# Revit family: Shower-Rainhead-KOHLER-WaterTile-K-98740_1
name_source: partatom
category: Plumbing Fixtures
revit_build: Autodesk Revit 2015 (Build: 20140606_1530(x64)
units: mm (PartAtom-declared; Revit-internal decimal feet)

## types (5) — shared parameters
ADA Compliant = No
Assembly Code = D2010700
CW Connection = No
Cold Water Inlet = Cold Water Inlet
Date Modified = 02/14/2019
Default Elevation = 0"
Description = Overhead shower panel with four 22-nozzle sprayheads
Drain Included = No
Flow Rate = 1 GPM
HW Connection = Yes
Height = 9 7/8"
Hot Water Inlet 1 = Tempered Water Inlet 1
Hot Water Inlet 2 = Tempered Water Inlet 2
Hot Water Inlet 3 = Tempered Water Inlet 3
Hot Water Inlet 4 = Tempered Water Inlet 4
Length = 2 5/8"
Manufacturer = KOHLER Co.
MasterFormat 1995 = 15410
MasterFormat 2004 = 22.41.23
Material = Premium Metal Construction
Panel Thickness = 0"
Pressure = 80.00 psi
Product Documentation Link = https://www.us.kohler.com
Product Name = WaterTile
Product Page URL = http://www.us.kohler.com
URL = https://www.us.kohler.com
Vent Connection = No
Waste Connection = No
Waste Water Outlet = Waste Water Outlet
WaterSense Certified = No
Width = 9 7/8"

## per-type parameters (varying)
| type | Finish | Model | Type |
| CP-Polished Chrome | Kohler-Metal-CP-Polished_Chrome | K-98740-CP | 1 |
| SN-Vibrant Polished Nickel | Kohler-Metal-SN-Vibrant_Polished_Nickel | K-98740-SN | 2 |
| BN-Vibrant Brushed Nickel | Kohler-Metal-BN-Vibrant_Brushed_Nickel | K-98740-BN | 3 |
| BV-Vibrant Brushed Bronze | Kohler-Metal-BV-Brushed_Bronze | K-98740-BV | 4 |
| 2BZ-Oil-Rubbed Bronze | Kohler-Metal-2BZ-Oil_Rubbed_Bronze | K-98740-2BZ | 5 |

## geometry (parser evidence)
native form markers: Sweep x5
no freeform markers — native parametric forms only
